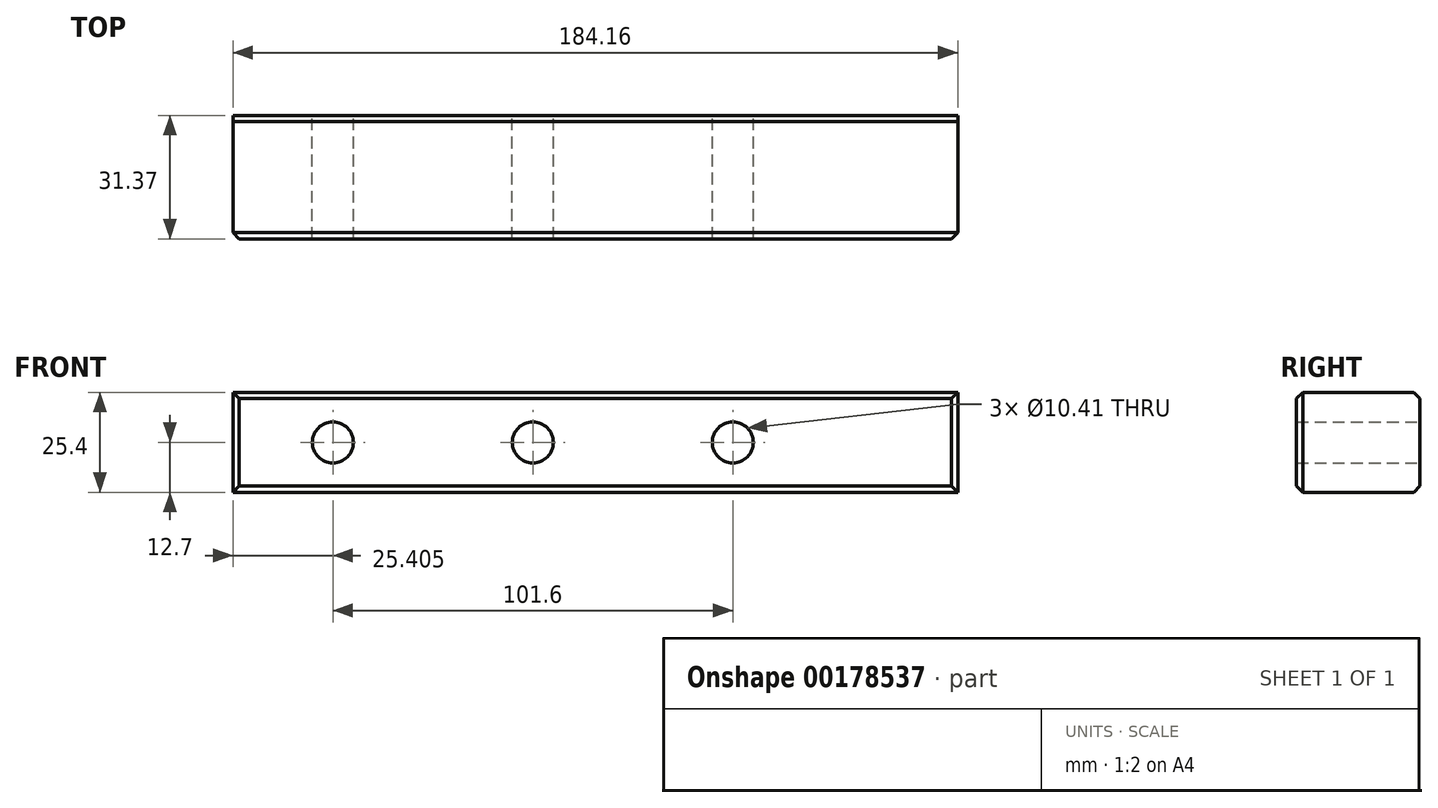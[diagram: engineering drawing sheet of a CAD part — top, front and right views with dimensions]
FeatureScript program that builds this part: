
annotation { "Feature Type Name" : "Feature", "Feature Type Description" : "" }
export const myFeature = defineFeature(function(context is Context, id is Id, definition is map)
    precondition{}
    {
        {
            var Q0;
            Q0=qCreatedBy(makeId("Front.planeOp"),FACE);
            var sketch = newSketch(context, id + "F0", { "sketchPlane" : qUnion([Q0])});
            skLineSegment(sketch, "E0.bottom", {"start": v(92.08, 12.7) * mm, "end": v(-92.08, 12.7) * mm});
            skLineSegment(sketch, "E0.top", {"start": v(92.08, -12.7) * mm, "end": v(-92.08, -12.7) * mm});
            skLineSegment(sketch, "E0.left", {"start": v(92.08, 12.7) * mm, "end": v(92.08, -12.7) * mm});
            skLineSegment(sketch, "E0.right", {"start": v(-92.08, 12.7) * mm, "end": v(-92.08, -12.7) * mm});
            skPoint(sketch, "E0.middle", {"position": v(0, 0) * mm});
            skCircle(sketch, "E1", {"center": v(34.92, 0) * mm, "radius": 5.2 * mm});
            skPoint(sketch, "E1.centerSnap0", {"position": v(92.08, 0) * mm});
            skCircle(sketch, "E2.1.0.0", {"center": v(-15.88, 0) * mm, "radius": 5.2 * mm});
            skCircle(sketch, "E2.2.0.0", {"center": v(-66.68, 0) * mm, "radius": 5.2 * mm});
            skLineSegment(sketch, "E2.direction1", {"start": v(34.92, 0) * mm, "end": v(-15.88, 0) * mm, "construction": true});
            skLineSegment(sketch, "E3.direction1", {"start": v(60.33, 0) * mm, "end": v(9.52, 0) * mm, "construction": true});
            skSolve(sketch);
        }
        {
            var Q0;
            Q0 = qSketchRegion(id + "F0", true);
            extrude(context, id + "F1", {"entities" : qUnion([Q0]), "depth" : 31.37 * mm});
        }
        {
            var Q0;
            Q0=makeQuery(id+"F1.opExtrude","CAP_EDGE",EDGE,{"disambiguationData":[OSD([sQuery(id+"F0.wireOp",EDGE,"E0.left")])],"isStart":false});
            chamfer(context, id + "F2", {"entities" : qUnion([Q0]), "width" : 1.59 * mm, "tangentPropagation" : true});
        }
        {
            var Q0;
            Q0=makeQuery(id+"F1.opExtrude","CAP_EDGE",EDGE,{"disambiguationData":[OSD([sQuery(id+"F0.wireOp",EDGE,"E0.right")])],"isStart":false});
            chamfer(context, id + "F3", {"entities" : qUnion([Q0]), "width" : 1.59 * mm, "tangentPropagation" : true});
        }
        {
            var Q0;
            Q0=makeQuery(id+"F1.opExtrude","CAP_EDGE",EDGE,{"disambiguationData":[OSD([sQuery(id+"F0.wireOp",EDGE,"E0.bottom")])],"isStart":false});
            var Q1;
            Q1=makeQuery(id+"F1.opExtrude","CAP_EDGE",EDGE,{"disambiguationData":[OSD([sQuery(id+"F0.wireOp",EDGE,"E0.top")])],"isStart":false});
            var Q2;
            Q2=makeQuery(id+"F1.opExtrude","CAP_EDGE",EDGE,{"disambiguationData":[OSD([sQuery(id+"F0.wireOp",EDGE,"E0.top")])],"isStart":true});
            var Q3;
            Q3=makeQuery(id+"F1.opExtrude","CAP_EDGE",EDGE,{"disambiguationData":[OSD([sQuery(id+"F0.wireOp",EDGE,"E0.bottom")])],"isStart":true});
            chamfer(context, id + "F4", {"entities" : qUnion([Q0, Q1, Q2, Q3]), "width" : 1.59 * mm, "tangentPropagation" : true});
        }
    });
